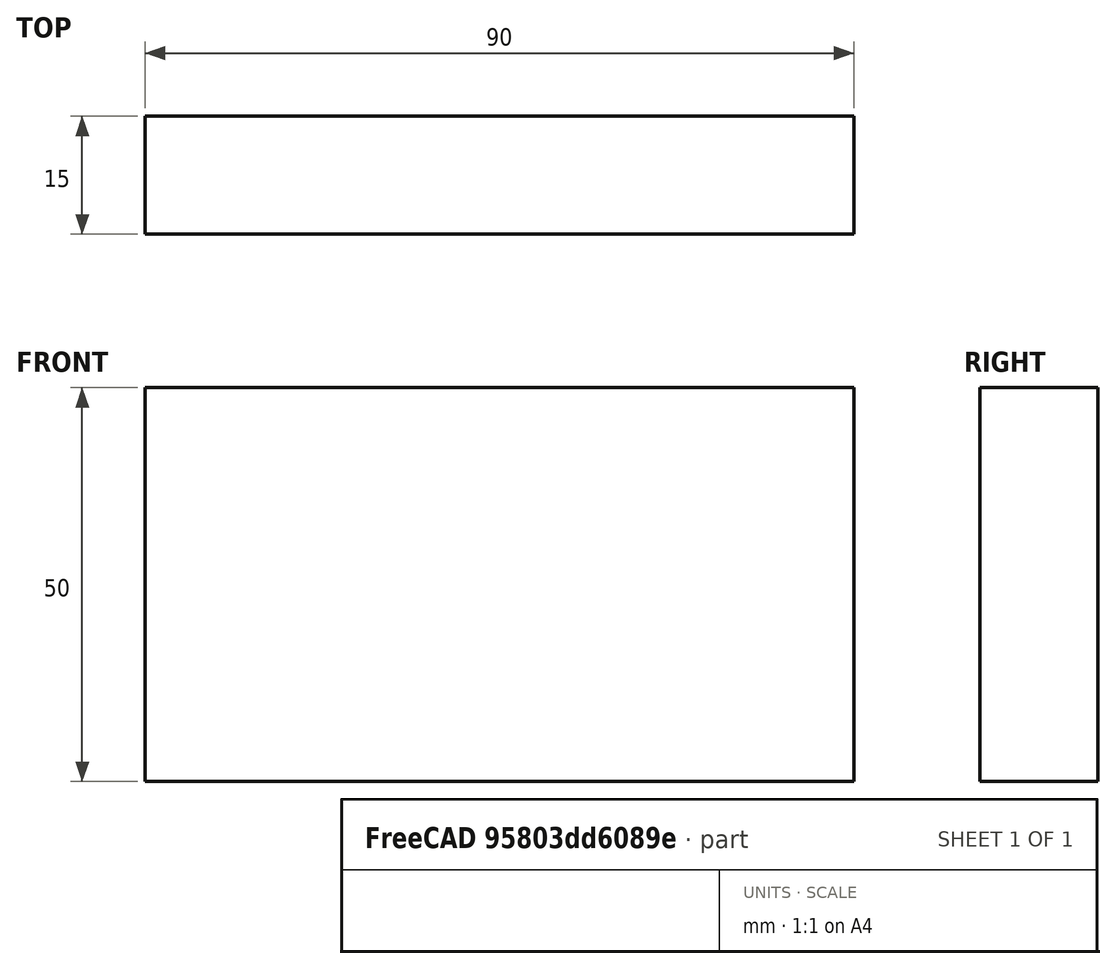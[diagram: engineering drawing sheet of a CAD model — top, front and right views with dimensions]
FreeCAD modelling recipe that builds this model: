
FCSTD DOCUMENT  (FreeCAD 0.15R4671 (Git))
Label: Flat Bar 90x15 EN10058 S235JR
License: All rights reserved
LicenseURL: http://en.wikipedia.org/wiki/All_rights_reserved
objects: Sketcher::SketchObject×1, Part::Extrusion×1
note: 2 computed .brp shape members not serialized (recipe doc carries the construction recipe); baked Part::Feature solids carry a one-line shape summary decoded from their .brp

FEATURE [Sketcher::SketchObject] Sketch
  sketch-geometry (4):
    g0: LineSegment StartX=-45 StartY=-7.5 StartZ=0 EndX=45 EndY=-7.5 EndZ=0
    g1: LineSegment StartX=45 StartY=-7.5 StartZ=0 EndX=45 EndY=7.5 EndZ=0
    g2: LineSegment StartX=45 StartY=7.5 StartZ=0 EndX=-45 EndY=7.5 EndZ=0
    g3: LineSegment StartX=-45 StartY=7.5 StartZ=0 EndX=-45 EndY=-7.5 EndZ=0
  constraints (12):
    c: Coincident(g0,g1)
    c: Coincident(g1,g2)
    c: Coincident(g2,g3)
    c: Coincident(g3,g0)
    c: Horizontal(g0)
    c: Horizontal(g2)
    c: Vertical(g1)
    c: Vertical(g3)
    c: Symmetric(g1,g2,g-2)
    c: Symmetric(g0,g1,g-1)
    c: DistanceY(g1) = 15
    c: DistanceX(g0) = 90
FEATURE [Part::Extrusion] Extrude  label="Flat Bar 90x15 EN10058 S235JR"
  Base = -> Sketch
  Dir = (0,0,50)
  Solid = true
